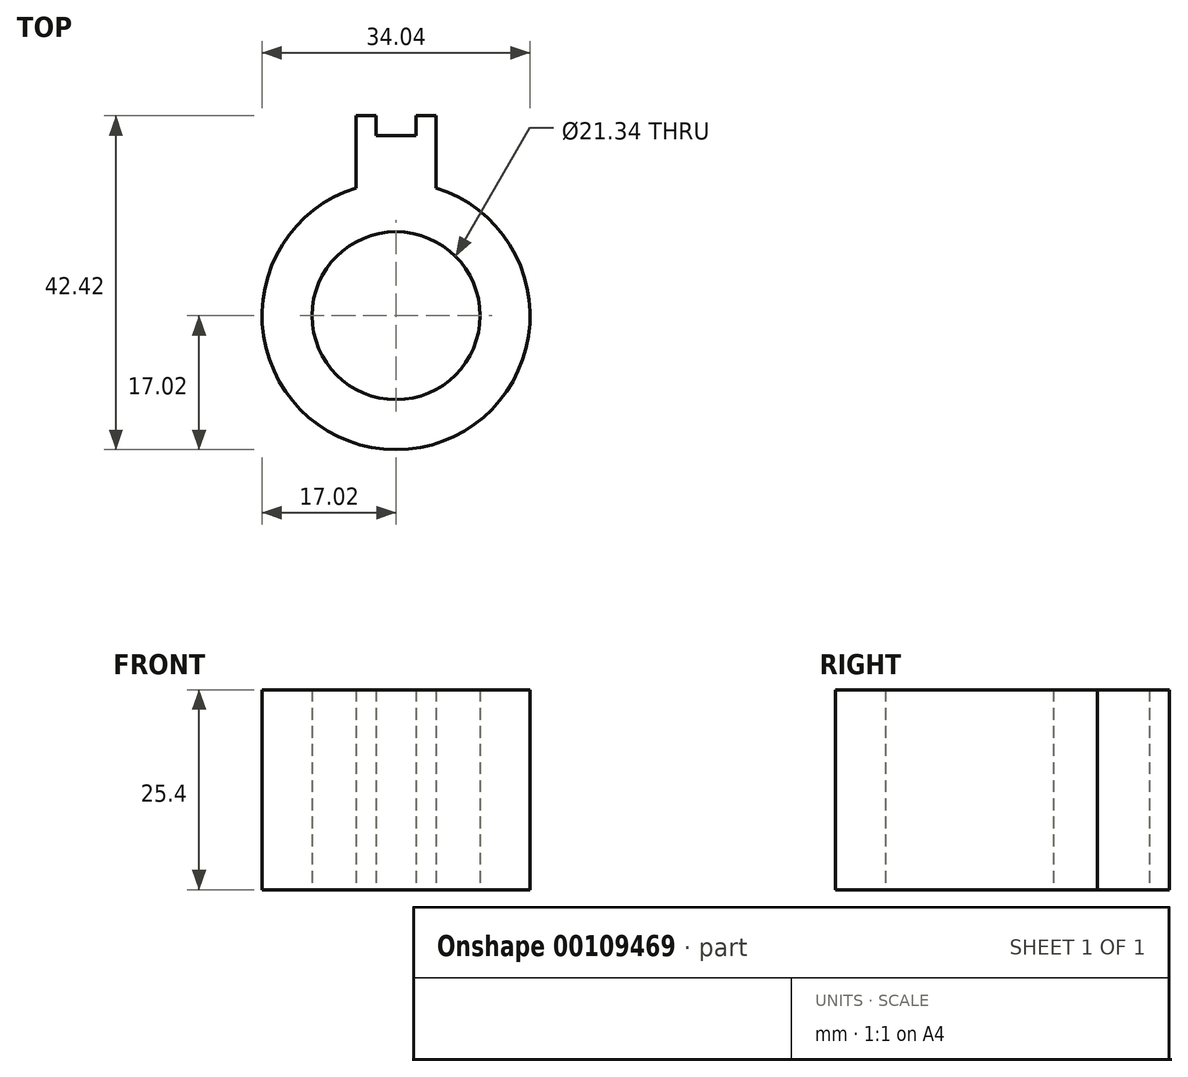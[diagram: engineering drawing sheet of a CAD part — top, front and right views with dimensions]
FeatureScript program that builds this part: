
annotation { "Feature Type Name" : "Feature", "Feature Type Description" : "" }
export const myFeature = defineFeature(function(context is Context, id is Id, definition is map)
    precondition{}
    {
        {
            var Q0;
            Q0=qCreatedBy(makeId("Top.planeOp"),FACE);
            var sketch = newSketch(context, id + "F0", { "sketchPlane" : qUnion([Q0])});
            skCircle(sketch, "E0", {"center": v(0, 0) * mm, "radius": 10.67 * mm});
            skArc(sketch, "E1", {"start": v(-5.08, 16.24) * mm, "mid": v(0, -17.02) * mm, "end": v(5.08, 16.24) * mm});
            skLineSegment(sketch, "E2.bottom", {"start": v(5.08, 25.4) * mm, "end": v(2.54, 25.4) * mm});
            skLineSegment(sketch, "E2.left", {"start": v(5.08, 25.4) * mm, "end": v(5.08, 16.24) * mm});
            skLineSegment(sketch, "E2.right", {"start": v(2.54, 25.4) * mm, "end": v(2.54, 22.86) * mm});
            skLineSegment(sketch, "E3.bottom", {"start": v(-2.54, 25.4) * mm, "end": v(-5.08, 25.4) * mm});
            skLineSegment(sketch, "E3.left", {"start": v(-2.54, 25.4) * mm, "end": v(-2.54, 22.86) * mm});
            skLineSegment(sketch, "E3.right", {"start": v(-5.08, 25.4) * mm, "end": v(-5.08, 16.24) * mm});
            skLineSegment(sketch, "E4", {"start": v(-2.54, 22.86) * mm, "end": v(2.54, 22.86) * mm});
            skSolve(sketch);
        }
        {
            var Q0;
            Q0 = qSketchRegion(id + "F0", true);
            extrude(context, id + "F1", {"entities" : qUnion([Q0]), "depth" : 25.4 * mm});
        }
    });
